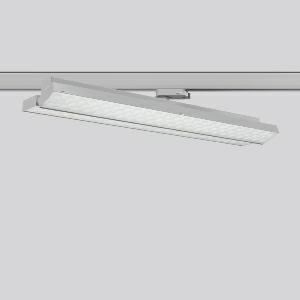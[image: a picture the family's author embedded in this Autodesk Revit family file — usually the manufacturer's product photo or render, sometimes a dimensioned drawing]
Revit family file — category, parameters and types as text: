
# Revit family: tx-move_742161_004_1_0425
name_source: partatom
category: Lighting Fixtures
units: mm (PartAtom-declared; Revit-internal decimal feet)

## family parameters
Cut with Voids When Loaded = No
Host = Face
Light Source = No
Part Type = Normal
Room Calculation Point = No
Round Connector Dimension = Use Diameter
Shared = No

## types (1)
- MultiLumen 1 (1 x LED Modul 840, 3125 lm, 4000)
    Apparent Load = 41 VA
    CIE Flux Codes = 90 97 99 100 100
    Color Rendering = 80
    Color Temperature = 4000
    Default Elevation = 1800 mm
    Description = Series: TX-MOVE
Multifunctional surface-mounted spotlight for area lighting. Very flat design. Housing: sheet steel, powder-coated. Rotation range: 356°. Swivel range: 90°. Consistent alignment possible with visible tilt scale. High-efficiency LED units with optimum light control thanks to clear plastic (PC) lens optics. Spezielle Mikrostrukturen reduzieren Gelbsaum. Symmetrical light distribution. With multi adaptor for 3-circuit tracks 230 V. Suitable for Track on ceiling. MultiLumen: Luminous flux adjustable in 3 steps. Factory setting is the highest luminous flux. Environmentally friendly and resource-saving due to replaceable and recyclable components. Very good glare control, ideal for till areas. 
Colour: silver, matt (approx. RAL 9006)
Length: 570 mm
Width: 119 mm
Height: 92 mm
Lamp: LED
Socket: without socket
Colour temperature: 4000K
Colour rendering index (CRI): 80
System power: 41 W
Rated luminous flux: 6250 lm
Luminous efficiency: 152 lm/W
System power 2: 57 W
Rated luminous flux 2: 8450 lm
Luminous efficiency 2: 148 lm/W
System power 3: 73 W
Rated luminous flux 3: 10400 lm
Luminous efficiency 3: 142 lm/W
Control gear: Regulated power supply
Protection class: I
Type of protection: IP 20
    Height = 75 mm
    Lamp = 1 x LED Modul 840
    Lamp Light Flux = 3125 lm
    Lamp count = 1
    Length = 569 mm
    Lifetime = 50000 h
    Luminous efficacy = 152 lm/W
    Manufacturer = RZB
    ModVariant = No
    Model = 742161.004.1
    Mounting Place = Ceiling
    Mounting Type = Surface mounted
    Number of Poles = 1
    OnlyDefault = Yes
    Power Factor = 1
    Product Name = TX-MOVE
    Product group = Track mounted projectors
    ProductGroupID = 301
    Protection Class = Protection class I
    Protection Degree = IP 20
    RLX_Detail_Level = 1
    RLX_Emergency_Light_Flux = 0 lm
    RLX_Emergency_Type = 0
    RLX_Emergency_Type_DB = No
    RlxData = <blob elided: 33269 chars, md5=55b1e6f4>
    Socket = socket
    Standby Power = 0 W
    System Light Flux = 6250 lm
    System Power = 41 W
    Type Comments = MultiLumen 1
    Type Image = 742162.004.jpg
    URL = http://relux.com
    VarID = multilumen_1
    Voltage = 0 V
    Weight = 0.00 kg
    Width = 119 mm

## geometry (parser evidence)
native form markers: Blend x4, Sweep x15
no freeform markers — native parametric forms only
